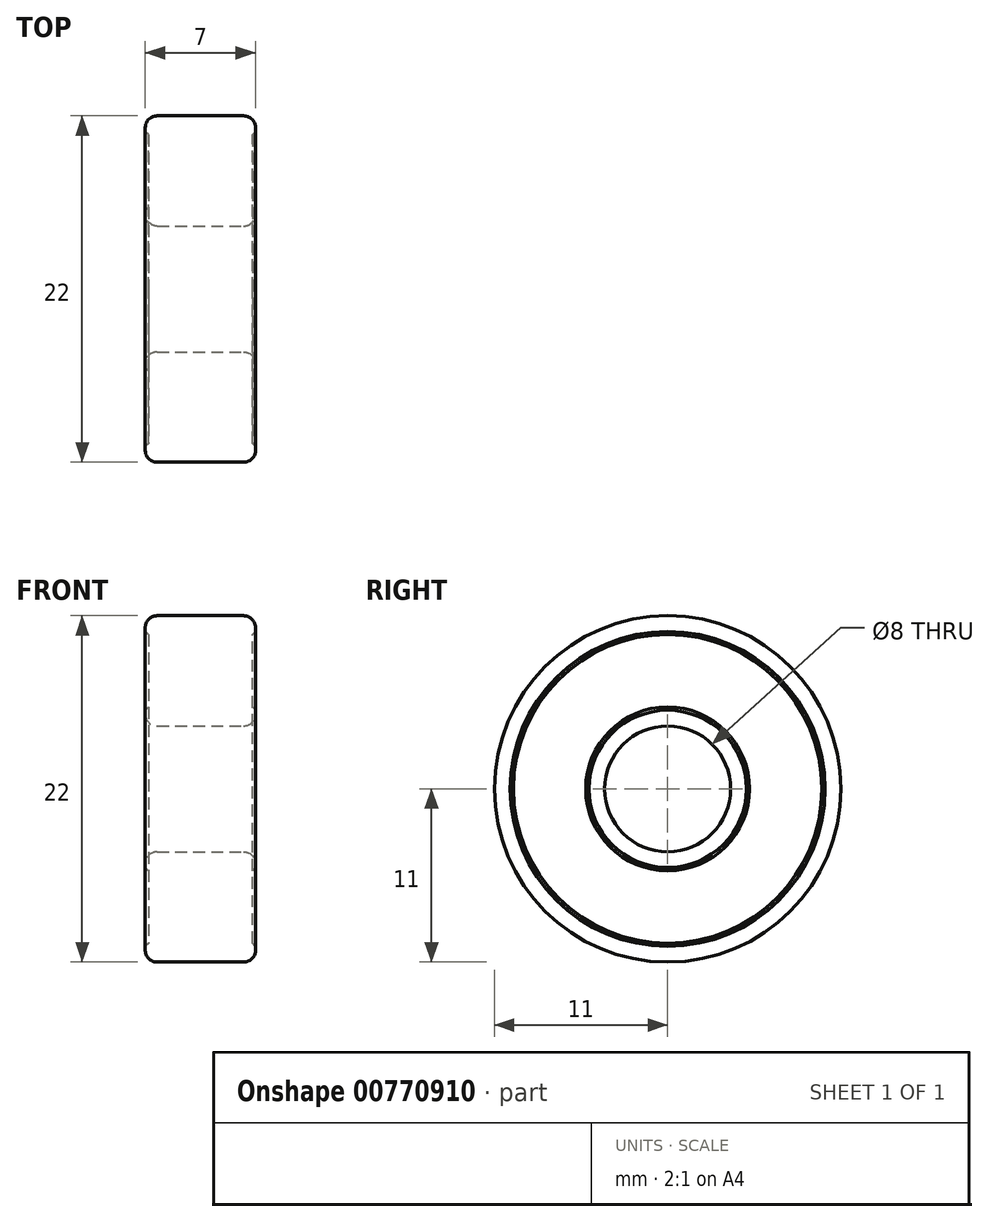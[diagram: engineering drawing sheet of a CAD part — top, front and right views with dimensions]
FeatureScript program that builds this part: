
annotation { "Feature Type Name" : "Feature", "Feature Type Description" : "" }
export const myFeature = defineFeature(function(context is Context, id is Id, definition is map)
    precondition{}
    {
        {
            var Q0;
            Q0=qCreatedBy(makeId("Front.planeOp"),FACE);
            var sketch = newSketch(context, id + "F0", { "sketchPlane" : qUnion([Q0])});
            skLineSegment(sketch, "E0.bottom", {"start": v(-3.5, 11) * mm, "end": v(3.5, 11) * mm});
            skLineSegment(sketch, "E0.top", {"start": v(-3.5, 4) * mm, "end": v(3.5, 4) * mm});
            skLineSegment(sketch, "E0.left", {"start": v(-3.5, 11) * mm, "end": v(-3.5, 4) * mm});
            skLineSegment(sketch, "E0.right", {"start": v(3.5, 11) * mm, "end": v(3.5, 4) * mm});
            skPoint(sketch, "E1", {"position": v(0, 11) * mm});
            skLineSegment(sketch, "E2", {"start": v(5.31, 0) * mm, "end": v(-6.65, 0) * mm, "construction": true});
            skSolve(sketch);
        }
        {
            var Q0;
            Q0=qSketchRegion(id+"F0",true);
            var Q1;
            Q1=sQuery(id+"F0.wireOp",EDGE,"E2");
            revolve(context, id + "F1", {"entities" : qUnion([Q0]), "axis" : qUnion([Q1]), "revolveType" : RevolveType.FULL});
        }
        {
            var Q0;
            Q0=makeQuery(id+"F1.opRevolve","SWEPT_EDGE",EDGE,{"disambiguationData":[OSD([sQuery(id+"F0.wireOp",EDGE,"E0.bottom"),sQuery(id+"F0.wireOp",EDGE,"E0.left")])]});
            var Q1;
            Q1=makeQuery(id+"F1.opRevolve","SWEPT_EDGE",EDGE,{"disambiguationData":[OSD([sQuery(id+"F0.wireOp",EDGE,"E0.top"),sQuery(id+"F0.wireOp",EDGE,"E0.left")])]});
            var Q2;
            Q2=makeQuery(id+"F1.opRevolve","SWEPT_EDGE",EDGE,{"disambiguationData":[OSD([sQuery(id+"F0.wireOp",EDGE,"E0.bottom"),sQuery(id+"F0.wireOp",EDGE,"E0.right")])]});
            var Q3;
            Q3=makeQuery(id+"F1.opRevolve","SWEPT_EDGE",EDGE,{"disambiguationData":[OSD([sQuery(id+"F0.wireOp",EDGE,"E0.top"),sQuery(id+"F0.wireOp",EDGE,"E0.right")])]});
            fillet(context, id + "F2", {"entities" : qUnion([Q0, Q1, Q2, Q3]), "radius" : 0.75 * mm, "tangentPropagation" : true, "allowEdgeOverflow" : false});
        }
        {
            var Q0;
            Q0=qCreatedBy(makeId("Top.planeOp"),FACE);
            var sketch = newSketch(context, id + "F3", { "sketchPlane" : qUnion([Q0])});
            skLineSegment(sketch, "E3", {"start": v(-5.02, 0) * mm, "end": v(5.29, 0) * mm});
            skLineSegment(sketch, "E4", {"start": v(-3.5, -10) * mm, "end": v(-3.3, -10) * mm});
            skLineSegment(sketch, "E5", {"start": v(-3.3, -10) * mm, "end": v(-3.3, -5) * mm});
            skLineSegment(sketch, "E6", {"start": v(-3.3, -5) * mm, "end": v(-3.5, -5) * mm});
            skLineSegment(sketch, "E7", {"start": v(-3.5, -5) * mm, "end": v(-3.5, -10) * mm});
            skLineSegment(sketch, "E8", {"start": v(3.3, -10) * mm, "end": v(3.5, -10) * mm});
            skPoint(sketch, "E8.startSnap0", {"position": v(-3.4, -10) * mm});
            skLineSegment(sketch, "E9", {"start": v(3.5, -10) * mm, "end": v(3.5, -5) * mm});
            skLineSegment(sketch, "E10", {"start": v(3.5, -5) * mm, "end": v(3.3, -5) * mm});
            skLineSegment(sketch, "E11", {"start": v(3.3, -5) * mm, "end": v(3.3, -10) * mm});
            skSolve(sketch);
        }
        {
            var Q0;
            Q0=qSketchRegion(id+"F3",true);
            var Q1;
            Q1=sQuery(id+"F3.wireOp",EDGE,"E3");
            revolve(context, id + "F4", {"operationType" : NewBodyOperationType.REMOVE, "surfaceOperationType" : NewSurfaceOperationType.NEW, "entities" : qUnion([Q0]), "axis" : qUnion([Q1]), "revolveType" : RevolveType.FULL, "oppositeDirection" : true});
        }
        {
            var Q0;
            Q0=makeQuery(id+"F4.boolean.opBoolean","COPY",EDGE,{"derivedFrom":makeQuery(id+"F4.opRevolve","SWEPT_EDGE",EDGE,{"disambiguationData":[OSD([sQuery(id+"F3.wireOp",EDGE,"E4"),sQuery(id+"F3.wireOp",EDGE,"E5")])]})});
            var Q1;
            Q1=makeQuery(id+"F4.boolean.opBoolean","COPY",EDGE,{"derivedFrom":makeQuery(id+"F4.opRevolve","SWEPT_EDGE",EDGE,{"disambiguationData":[OSD([sQuery(id+"F3.wireOp",EDGE,"E5"),sQuery(id+"F3.wireOp",EDGE,"E6")])]})});
            var Q2;
            Q2=makeQuery(id+"F4.boolean.opBoolean","COPY",EDGE,{"derivedFrom":makeQuery(id+"F4.opRevolve","SWEPT_EDGE",EDGE,{"disambiguationData":[OSD([sQuery(id+"F3.wireOp",EDGE,"E8"),sQuery(id+"F3.wireOp",EDGE,"E11")])]})});
            var Q3;
            Q3=makeQuery(id+"F4.boolean.opBoolean","COPY",EDGE,{"derivedFrom":makeQuery(id+"F4.opRevolve","SWEPT_EDGE",EDGE,{"disambiguationData":[OSD([sQuery(id+"F3.wireOp",EDGE,"E10"),sQuery(id+"F3.wireOp",EDGE,"E11")])]})});
            chamfer(context, id + "F5", {"entities" : qUnion([Q0, Q1, Q2, Q3]), "width" : .2 * mm, "tangentPropagation" : true});
        }
    });
